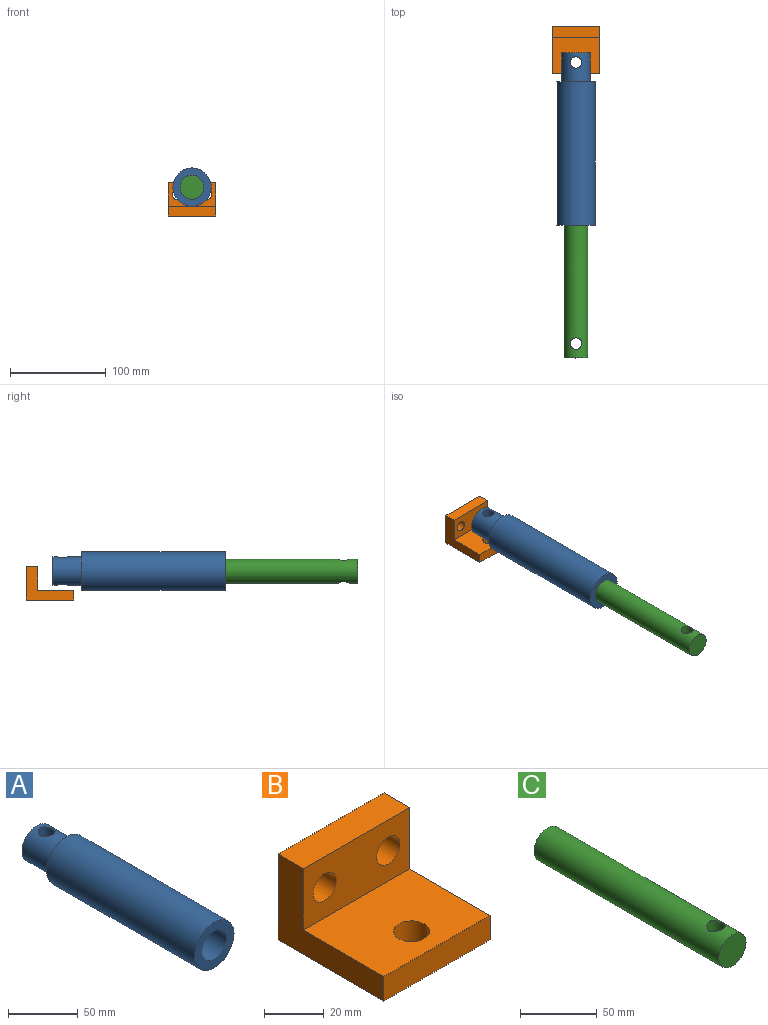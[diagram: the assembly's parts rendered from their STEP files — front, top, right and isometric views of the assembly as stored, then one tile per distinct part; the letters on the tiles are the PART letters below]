
ASSEMBLY  parts=3 mates=2
PART A: 8 faces, bbox 40x180x40 mm
  f0: cylinder r=12.5mm len=140mm, axis (0,1,0), area 10995.6mm2, adj f2,f3
  f1: cylinder r=20mm len=150mm, axis (0,1,0), area 18849.6mm2, adj f2,f4
  f2: plane 40x40mm, normal (0,-1,0), area 765.8mm2, adj f0,f1
  f3: plane 25x25mm, normal (0,-1,0), area 490.9mm2, adj f0
  f4: plane 40x40mm, normal (0,1,0), area 549.8mm2, adj f1,f5
  f5: cylinder r=15mm len=30mm, axis (0,-1,0), area 2596.3mm2, adj f4,f6,f7
  f6: plane 30x30mm, normal (0,1,0), area 706.9mm2, adj f5
  f7: cylinder r=6mm len=30mm, axis (0,0,1), area 1084.3mm2, adj f5
PART B: 11 faces, bbox 50x50x35 mm
  f0: plane 50x38mm, normal (0,0,1), area 1786.9mm2, adj f1,f2,f4,f5,f7
  f1: plane 50x10mm, normal (0,-1,0), area 500mm2, adj f0,f2,f5,f6
  f2: plane 50x35mm, normal (1,0,0), area 800mm2, adj f0,f1,f3,f6,f7,f8
  f3: plane 50x35mm, normal (0,1,0), area 1559.9mm2, adj f2,f5,f6,f8,f9,f10
  f4: cylinder r=6mm len=12mm, axis (0,0,-1), area 377mm2, adj f0,f6
  f5: plane 50x35mm, normal (-1,0,0), area 800mm2, adj f0,f1,f3,f6,f7,f8
  f6: plane 50x50mm, normal (0,0,-1), area 2386.9mm2, adj f1,f2,f3,f4,f5
  f7: plane 50x25mm, normal (0,-1,0), area 1059.9mm2, adj f0,f2,f5,f8,f9,f10
  f8: plane 50x12mm, normal (0,0,1), area 600mm2, adj f2,f3,f5,f7
  f9: cylinder r=5.5mm len=12mm, axis (0,-1,0), area 414.7mm2, adj f3,f7
  f10: cylinder r=5.5mm len=12mm, axis (0,-1,0), area 414.7mm2, adj f3,f7
PART C: 4 faces, bbox 25x170x25 mm
  f0: cylinder r=12.5mm len=170mm, axis (0,1,0), area 13118.9mm2, adj f1,f2,f3
  f1: plane 25x25mm, normal (0,-1,0), area 490.9mm2, adj f0
  f2: plane 25x25mm, normal (0,1,0), area 490.9mm2, adj f0
  f3: cylinder r=6mm len=25mm, axis (0,0,1), area 885.6mm2, adj f0
PLACE A t=(-11.37,35.15,34.94)mm
PLACE B t=(-11.37,35.15,-25.25)mm
PLACE C t=(-11.37,76.73,34.94)mm
MATE revolute B.f4 <-> A.f7  axis (0,0,1) through (-11.37,65.15,14.75)mm
MATE slider C.f0 <-> A.f0  axis (0,1,0) through (-11.37,-73.27,34.94)mm
